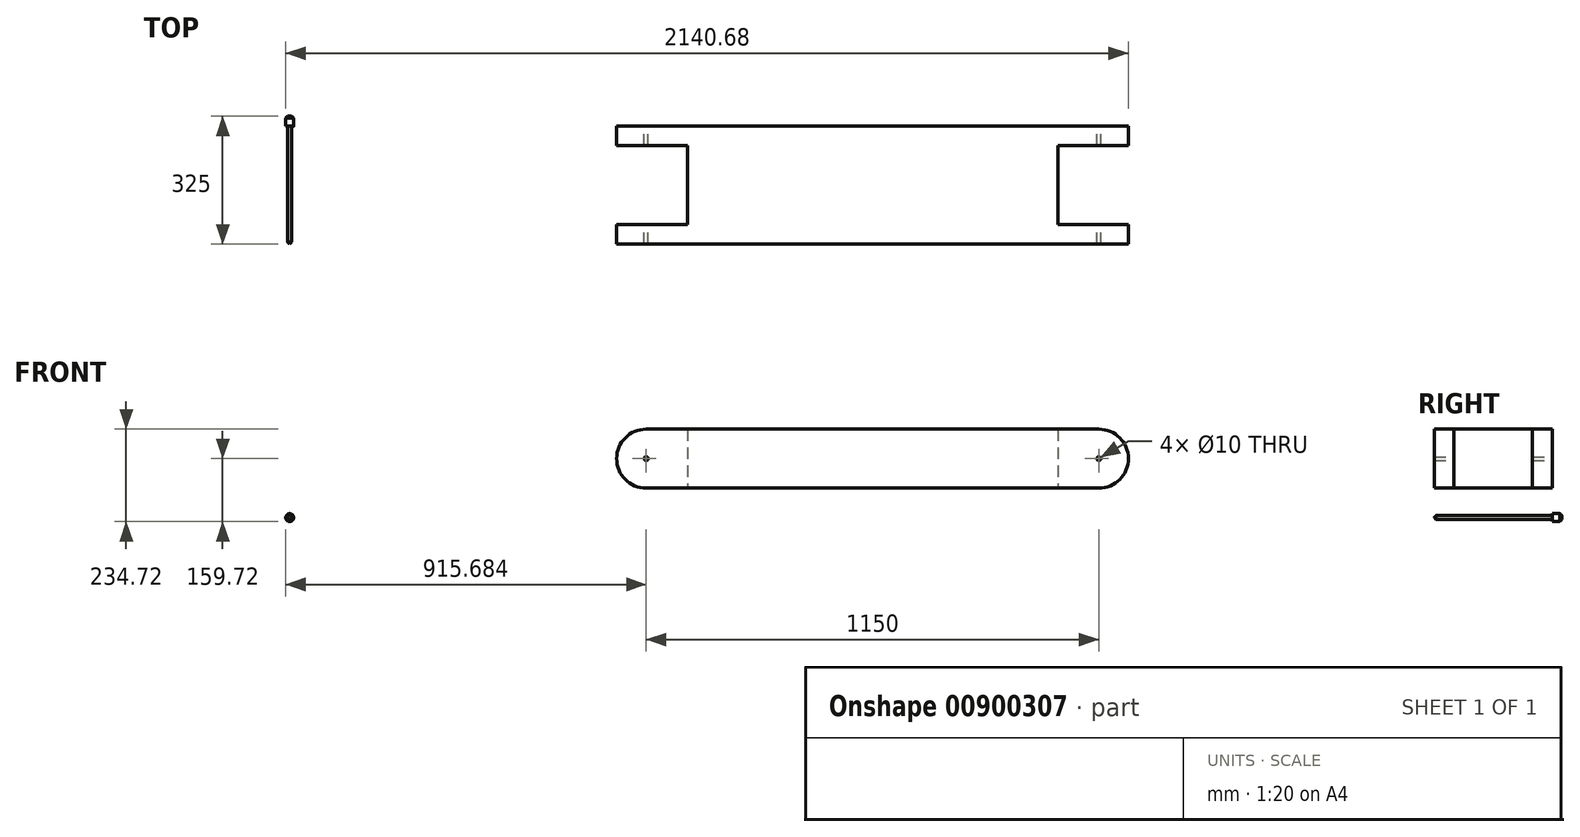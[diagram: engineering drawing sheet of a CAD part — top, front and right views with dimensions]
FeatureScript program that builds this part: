
annotation { "Feature Type Name" : "Feature", "Feature Type Description" : "" }
export const myFeature = defineFeature(function(context is Context, id is Id, definition is map)
    precondition{}
    {
        {
            var Q0;
            Q0=qCreatedBy(makeId("Front.planeOp"),FACE);
            var sketch = newSketch(context, id + "F0", { "sketchPlane" : qUnion([Q0])});
            skLineSegment(sketch, "E0.bottom", {"start": v(-28.77, 150) * mm, "end": v(1121.23, 150) * mm});
            skLineSegment(sketch, "E0.top", {"start": v(-28.77, 0) * mm, "end": v(1121.23, 0) * mm});
            skLineSegment(sketch, "E0.left", {"start": v(-103.77, 75) * mm, "end": v(-103.77, 75) * mm});
            skLineSegment(sketch, "E0.right", {"start": v(1196.23, 75) * mm, "end": v(1196.23, 75) * mm});
            skPoint(sketch, "E1.visualSharp", {"position": v(1196.23, 150) * mm});
            skArc(sketch, "E1.filletArc", {"start": v(1196.23, 75) * mm, "mid": v(1174.27, 128.03) * mm, "end": v(1121.23, 150) * mm});
            skPoint(sketch, "E2.visualSharp", {"position": v(1196.23, 0) * mm});
            skArc(sketch, "E2.filletArc", {"start": v(1121.23, 0) * mm, "mid": v(1174.27, 21.97) * mm, "end": v(1196.23, 75) * mm});
            skPoint(sketch, "E3.visualSharp", {"position": v(-103.77, 150) * mm});
            skArc(sketch, "E3.filletArc", {"start": v(-28.77, 150) * mm, "mid": v(-81.8, 128.03) * mm, "end": v(-103.77, 75) * mm});
            skPoint(sketch, "E4.visualSharp", {"position": v(-103.77, 0) * mm});
            skArc(sketch, "E4.filletArc", {"start": v(-103.77, 75) * mm, "mid": v(-81.8, 21.97) * mm, "end": v(-28.77, 0) * mm});
            skCircle(sketch, "E5", {"center": v(-28.77, 75) * mm, "radius": 5 * mm});
            skCircle(sketch, "E6", {"center": v(1121.23, 75) * mm, "radius": 5 * mm});
            skLineSegment(sketch, "E7", {"start": v(1016.8, 150) * mm, "end": v(1016.8, 0) * mm});
            skLineSegment(sketch, "E8", {"start": v(546.23, 150) * mm, "end": v(546.23, 0) * mm});
            skLineSegment(sketch, "E9.MirrorCS", {"start": v(75.66, 150) * mm, "end": v(75.66, 0) * mm});
            skSolve(sketch);
        }
        {
            var Q0;
            {var subQ0=sQuery(id+"F0.wireOp",EDGE,"E7");Q0=makeQuery(id+"F0.imprint","IMPRINT",FACE,{"disambiguationData":[TD([[makeQuery(id+"F0.imprint","IMPRINT",EDGE,{"derivedFrom":subQ0}),-1.0]])]});}
            var Q1;
            {var subQ0=sQuery(id+"F0.wireOp",EDGE,"E8");Q1=makeQuery(id+"F0.imprint","IMPRINT",FACE,{"disambiguationData":[TD([[makeQuery(id+"F0.imprint","IMPRINT",EDGE,{"derivedFrom":subQ0}),-1.0]])]});}
            extrude(context, id + "F1", {"entities" : qUnion([Q0, Q1]), "depth" : 150 * mm, "offsetDistance" : 25 * mm});
        }
        {
            var Q0;
            Q0=makeQuery(id+"F1.opExtrude","CAP_FACE",FACE,{"disambiguationData":[OSD([sQuery(id+"F0.wireOp",EDGE,"E0.bottom"),sQuery(id+"F0.wireOp",EDGE,"E0.top"),sQuery(id+"F0.wireOp",EDGE,"E7"),sQuery(id+"F0.wireOp",EDGE,"E9.MirrorCS")])],"isStart":true});
            extrude(context, id + "F2", {"entities" : qUnion([Q0]), "operationType" : NewBodyOperationType.ADD, "depth" : 150 * mm, "offsetDistance" : 25 * mm});
        }
        {
            var Q0;
            {var subQ1=sQuery(id+"F0.wireOp",EDGE,"E3.filletArc");Q0=makeQuery(id+"F0.imprint","IMPRINT",FACE,{"disambiguationData":[TD([[makeQuery(id+"F0.imprint","IMPRINT",EDGE,{"derivedFrom":subQ1}),1.0]])]});}
            extrude(context, id + "F3", {"entities" : qUnion([Q0]), "operationType" : NewBodyOperationType.ADD, "endBound" : BoundingType.SYMMETRIC, "depth" : 300 * mm, "offsetDistance" : 25 * mm});
        }
        {
            var Q0;
            {var subQ1=sQuery(id+"F0.wireOp",EDGE,"E3.filletArc");Q0=makeQuery(id+"F0.imprint","IMPRINT",FACE,{"disambiguationData":[TD([[makeQuery(id+"F0.imprint","IMPRINT",EDGE,{"derivedFrom":subQ1}),1.0]])]});}
            extrude(context, id + "F4", {"entities" : qUnion([Q0]), "operationType" : NewBodyOperationType.REMOVE, "endBound" : BoundingType.SYMMETRIC, "oppositeDirection" : true, "depth" : 200 * mm, "offsetDistance" : 25 * mm});
        }
        {
            var Q0;
            {var subQ3=sQuery(id+"F0.wireOp",EDGE,"E1.filletArc");Q0=makeQuery(id+"F0.imprint","IMPRINT",FACE,{"disambiguationData":[TD([[makeQuery(id+"F0.imprint","IMPRINT",EDGE,{"derivedFrom":subQ3}),1.0]])]});}
            extrude(context, id + "F5", {"entities" : qUnion([Q0]), "operationType" : NewBodyOperationType.ADD, "endBound" : BoundingType.SYMMETRIC, "depth" : 300 * mm, "offsetDistance" : 25 * mm});
        }
        {
            var Q0;
            {var subQ3=sQuery(id+"F0.wireOp",EDGE,"E1.filletArc");Q0=makeQuery(id+"F0.imprint","IMPRINT",FACE,{"disambiguationData":[TD([[makeQuery(id+"F0.imprint","IMPRINT",EDGE,{"derivedFrom":subQ3}),1.0]])]});}
            extrude(context, id + "F6", {"entities" : qUnion([Q0]), "operationType" : NewBodyOperationType.REMOVE, "endBound" : BoundingType.SYMMETRIC, "oppositeDirection" : true, "depth" : 200 * mm, "offsetDistance" : 25 * mm});
        }
        {
            var Q0;
            Q0=qCreatedBy(makeId("Front.planeOp"),FACE);
            var sketch = newSketch(context, id + "F7", { "sketchPlane" : qUnion([Q0])});
            skCircle(sketch, "E10", {"center": v(-934.45, -74.72) * mm, "radius": 5 * mm});
            skSolve(sketch);
        }
        {
            var Q0;
            Q0 = qSketchRegion(id + "F7", true);
            extrude(context, id + "F8", {"entities" : qUnion([Q0]), "endBound" : BoundingType.SYMMETRIC, "depth" : 300 * mm, "offsetDistance" : 25 * mm});
        }
        {
            var Q0;
            Q0=makeQuery(id+"F8.opExtrude","CAP_EDGE",EDGE,{"disambiguationData":[OSD([sQuery(id+"F7.wireOp",EDGE,"E10")])],"isStart":false});
            chamfer(context, id + "F9", {"entities" : qUnion([Q0]), "width" : 5 * mm, "tangentPropagation" : true});
        }
        {
            var Q0;
            Q0=makeQuery(id+"F8.opExtrude","CAP_FACE",FACE,{"disambiguationData":[OSD([sQuery(id+"F7.wireOp",EDGE,"E10")])],"isStart":true});
            var sketch = newSketch(context, id + "F10", { "sketchPlane" : qUnion([Q0])});
            skCircle(sketch, "E11", {"center": v(934.45, -74.72) * mm, "radius": 10 * mm});
            skSolve(sketch);
        }
        {
            var Q0;
            Q0 = qSketchRegion(id + "F10", true);
            extrude(context, id + "F11", {"entities" : qUnion([Q0]), "operationType" : NewBodyOperationType.ADD, "depth" : 25 * mm, "offsetDistance" : 25 * mm});
        }
        {
            var Q0;
            Q0=makeQuery(id+"F11.opExtrude","CAP_EDGE",EDGE,{"disambiguationData":[OSD([sQuery(id+"F10.wireOp",EDGE,"E11")])],"isStart":false});
            chamfer(context, id + "F12", {"entities" : qUnion([Q0]), "width" : 5 * mm, "tangentPropagation" : true});
        }
    });
